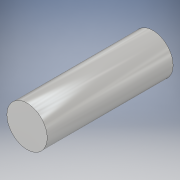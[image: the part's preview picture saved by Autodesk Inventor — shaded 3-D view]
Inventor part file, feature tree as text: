
AUTODESK INVENTOR PART (.ipt)
format: ipt  version: 2019.4 (Build 234330000, 330)  size: 95,744 bytes
history: native  units: mm
features: extrude x1, sketch x1
ambient origin geometry x8: Origin, YZ Plane, XZ Plane, XY Plane, X Axis, Y Axis, Z Axis, Center Point
bodies: Solid1 (feature_tree)
feature tree (2):
  extrude  "Extrusion1"  Depth=25.0mm TaperAngle=0.0deg
  sketch  "Sketch1"  dims[d0=8.0mm d1=25.0mm d2=0.0mm]
